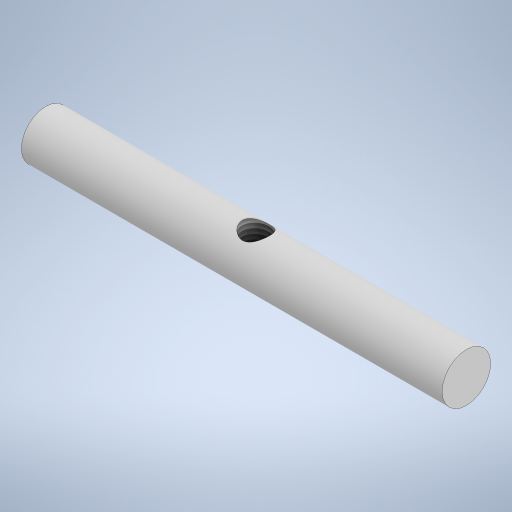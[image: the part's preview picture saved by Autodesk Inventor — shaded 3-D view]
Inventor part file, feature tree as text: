
AUTODESK INVENTOR PART (.ipt)
format: ipt  version: 2023 (Build 270158030, 158C)  size: 240,640 bytes
history: native  units: in
note: dims shown in document units (in); Inventor stores cm internally (conversion verified against a paired STEP export)
features: sketch x2, extrude x1, plane x1, hole x1
ambient origin geometry x8: Origin, YZ Plane, XZ Plane, XY Plane, X Axis, Y Axis, Z Axis, Center Point
bodies: Body1 (feature_tree)
feature tree (5):
  extrude  "Extrusion3"  Depth=5.1181in TaperAngle=0.0deg
  plane  "Work Plane1"
  hole  "Hole1"  [1 undecoded]
  sketch  "Sketch3"  dims[d6=0.5906in d7=5.1181in d8=0.0in]
  sketch  "Sketch6"  dims[d12=0.3298in d13=0.6299in d14=0.1575in d15=0.0787in d16=90.0deg d17=1.0748in d18=0.8108in]
note: 1 required parameter value undecoded (feature->parameter linkage not recoverable at this tier; creation-order binding heuristic only, values carry confidence <= 0.55)
